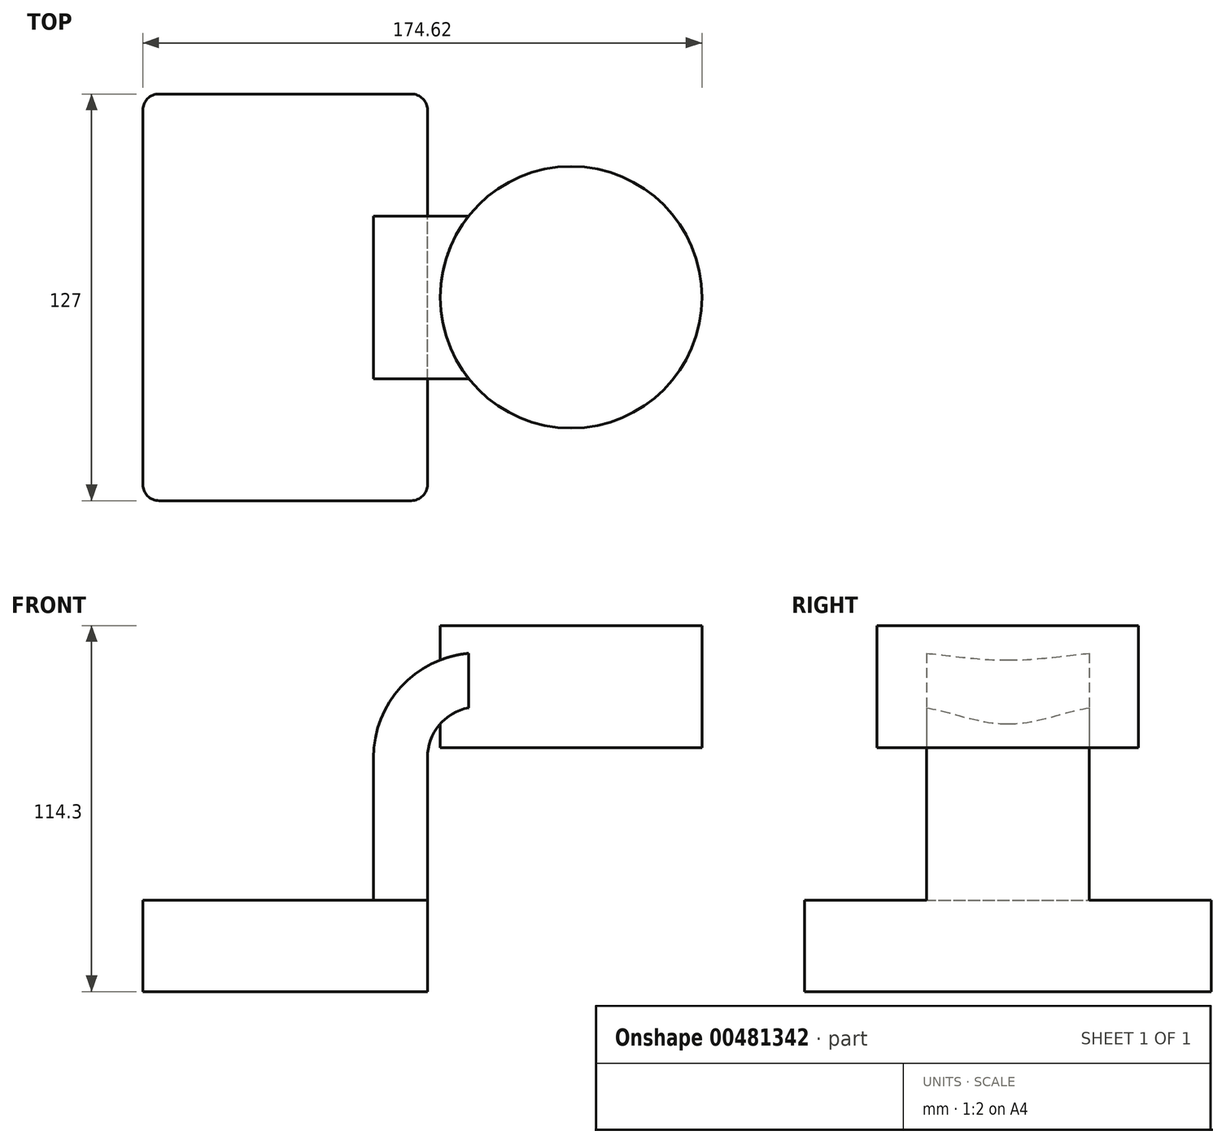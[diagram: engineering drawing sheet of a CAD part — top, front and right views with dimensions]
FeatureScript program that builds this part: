
annotation { "Feature Type Name" : "Feature", "Feature Type Description" : "" }
export const myFeature = defineFeature(function(context is Context, id is Id, definition is map)
    precondition{}
    {
        {
            var Q0;
            Q0=qCreatedBy(makeId("Front.planeOp"),FACE);
            var sketch = newSketch(context, id + "F0", { "sketchPlane" : qUnion([Q0])});
            skLineSegment(sketch, "E0.bottom", {"start": v(44.45, 14.29) * mm, "end": v(-44.45, 14.29) * mm});
            skLineSegment(sketch, "E0.top", {"start": v(44.45, -14.29) * mm, "end": v(-44.45, -14.29) * mm});
            skLineSegment(sketch, "E0.left", {"start": v(44.45, 14.29) * mm, "end": v(44.45, -14.29) * mm});
            skLineSegment(sketch, "E0.right", {"start": v(-44.45, 14.29) * mm, "end": v(-44.45, -14.29) * mm});
            skPoint(sketch, "E0.middle", {"position": v(0, 0) * mm});
            skLineSegment(sketch, "E1.bottom", {"start": v(66.67, 61.91) * mm, "end": v(130.17, 61.91) * mm});
            skLineSegment(sketch, "E1.top", {"start": v(66.67, 100.01) * mm, "end": v(130.17, 100.01) * mm});
            skLineSegment(sketch, "E1.left", {"start": v(66.67, 61.91) * mm, "end": v(66.67, 100.01) * mm});
            skLineSegment(sketch, "E1.right", {"start": v(130.17, 61.91) * mm, "end": v(130.17, 100.01) * mm});
            skPoint(sketch, "E1.middle", {"position": v(98.42, 80.96) * mm});
            skLineSegment(sketch, "E2", {"start": v(44.45, 14.29) * mm, "end": v(44.45, 58.74) * mm});
            skArc(sketch, "E3", {"start": v(44.45, 58.74) * mm, "mid": v(49.1, 69.96) * mm, "end": v(60.32, 74.61) * mm});
            skLineSegment(sketch, "E4", {"start": v(60.32, 74.61) * mm, "end": v(88.9, 74.61) * mm});
            skLineSegment(sketch, "E5.0", {"start": v(60.32, 91.46) * mm, "end": v(88.9, 91.46) * mm});
            skArc(sketch, "E5.1", {"start": v(27.6, 58.74) * mm, "mid": v(37.19, 81.88) * mm, "end": v(60.32, 91.46) * mm});
            skLineSegment(sketch, "E5.2", {"start": v(27.6, 14.29) * mm, "end": v(27.6, 58.74) * mm});
            skLineSegment(sketch, "E6", {"start": v(89.32, 61.91) * mm, "end": v(89.32, 100.01) * mm});
            skFitSpline(sketch, "E7", {"points": [v(-44.45, 14.29) * mm, v(60.32, 91.46) * mm], "startDerivative": vector(62.6, 121.23) * mm, "endDerivative": vector(123.77, -5.63) * mm});
            skSolve(sketch);
        }
        {
            var Q0;
            Q0=makeQuery(id+"F0.imprint","IMPRINT",FACE,{"disambiguationData":[TD([[makeQuery(id+"F0.imprint","IMPRINT",EDGE,{"derivedFrom":sQuery(id+"F0.wireOp",EDGE,"E0.top")}),-1.0]])]});
            extrude(context, id + "F1", {"entities" : qUnion([Q0]), "endBound" : BoundingType.SYMMETRIC, "depth" : 127 * mm});
        }
        {
            var Q0;
            {var subQ1=sQuery(id+"F0.wireOp",EDGE,"E2");Q0=makeQuery(id+"F0.imprint","IMPRINT",FACE,{"disambiguationData":[TD([[makeQuery(id+"F0.imprint","IMPRINT",EDGE,{"derivedFrom":subQ1}),1.0]])]});}
            var Q1;
            {var subQ6=sQuery(id+"F0.wireOp",EDGE,"E6");Q1=makeQuery(id+"F0.imprint","IMPRINT",FACE,{"disambiguationData":[TD([[makeQuery(id+"F0.imprint","IMPRINT",EDGE,{"derivedFrom":subQ6}),1.0]])]});}
            extrude(context, id + "F2", {"entities" : qUnion([Q0, Q1]), "operationType" : NewBodyOperationType.ADD, "endBound" : BoundingType.SYMMETRIC, "depth" : 50.8 * mm});
        }
        {
            var Q0;
            Q0=makeQuery(id+"F0.imprint","IMPRINT",FACE,{"disambiguationData":[TD([[makeQuery(id+"F0.imprint","IMPRINT",EDGE,{"derivedFrom":sQuery(id+"F0.wireOp",EDGE,"E5.1")}),1.0]])]});
            extrude(context, id + "F3", {"entities" : qUnion([Q0]), "operationType" : NewBodyOperationType.ADD, "endBound" : BoundingType.SYMMETRIC, "depth" : 25.4 * mm});
        }
        {
            var Q0;
            {var subQ0=sQuery(id+"F0.wireOp",EDGE,"E1.right");Q0=makeQuery(id+"F0.imprint","IMPRINT",FACE,{"disambiguationData":[TD([[makeQuery(id+"F0.imprint","IMPRINT",EDGE,{"derivedFrom":subQ0}),1.0]])]});}
            var Q1;
            Q1=sQuery(id+"F0.wireOp",EDGE,"E6");
            revolve(context, id + "F4", {"operationType" : NewBodyOperationType.ADD, "entities" : qUnion([Q0]), "axis" : qUnion([Q1]), "revolveType" : RevolveType.FULL});
        }
        {
            var Q0;
            Q0=makeQuery(id+"F1.opExtrude","CAP_EDGE",EDGE,{"disambiguationData":[OSD([sQuery(id+"F0.wireOp",EDGE,"E0.left")])],"isStart":false});
            var Q1;
            Q1=makeQuery(id+"F1.opExtrude","CAP_EDGE",EDGE,{"disambiguationData":[OSD([sQuery(id+"F0.wireOp",EDGE,"E0.right")])],"isStart":false});
            var Q2;
            Q2=makeQuery(id+"F1.opExtrude","CAP_EDGE",EDGE,{"disambiguationData":[OSD([sQuery(id+"F0.wireOp",EDGE,"E0.left")])],"isStart":true});
            var Q3;
            Q3=makeQuery(id+"F1.opExtrude","CAP_EDGE",EDGE,{"disambiguationData":[OSD([sQuery(id+"F0.wireOp",EDGE,"E0.right")])],"isStart":true});
            fillet(context, id + "F5", {"entities" : qUnion([Q0, Q1, Q2, Q3]), "radius" : 5.08 * mm, "tangentPropagation" : true, "allowEdgeOverflow" : false});
        }
    });
